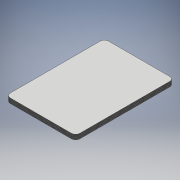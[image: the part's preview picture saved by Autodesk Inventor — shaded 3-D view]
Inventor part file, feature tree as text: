
AUTODESK INVENTOR PART (.ipt)
format: ipt  version: 2018 (Build 220112000, 112)  size: 196,096 bytes
history: native  units: mm
features: extrude x1, pattern_linear x1, sketch x1
ambient origin geometry x8: Origin, YZ Plane, XZ Plane, XY Plane, X Axis, Y Axis, Z Axis, Center Point
bodies: Solid1 (feature_tree)
feature tree (3):
  extrude  "Extrusion1"  Depth=89.0mm
  pattern_linear  "Rectangular Pattern1"  Spacing1=4.0mm  [1 undecoded]
  sketch  "Sketch1"  dims[d0=63.0mm d1=89.0mm d2=4.0mm d3=0.27mm d4=0.0mm d5=160.0mm d7=4.13mm]
note: 1 required parameter value undecoded (feature->parameter linkage not recoverable at this tier; creation-order binding heuristic only, values carry confidence <= 0.55)
